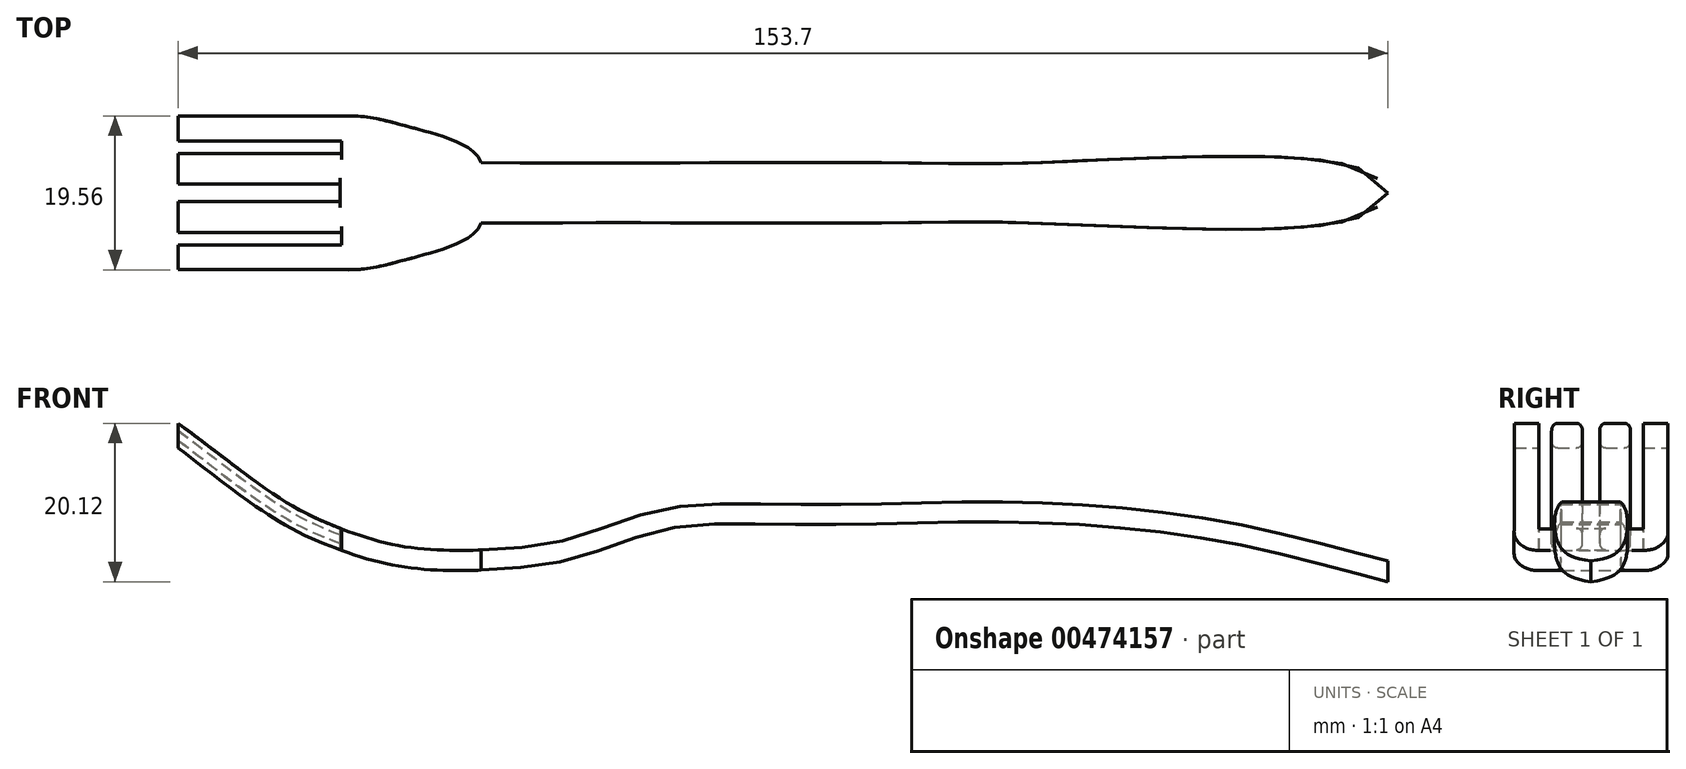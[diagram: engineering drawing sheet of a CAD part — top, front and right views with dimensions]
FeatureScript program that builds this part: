
annotation { "Feature Type Name" : "Feature", "Feature Type Description" : "" }
export const myFeature = defineFeature(function(context is Context, id is Id, definition is map)
    precondition{}
    {
        {
            var Q0;
            Q0=qCreatedBy(makeId("Front.planeOp"),FACE);
            var sketch = newSketch(context, id + "F0", { "sketchPlane" : qUnion([Q0])});
            skFitSpline(sketch, "E0", {"points": [v(0, 0) * mm, v(13.4, -9.82) * mm, v(20.96, -13.5) * mm, v(29.2, -15.74) * mm, v(40.7, -16) * mm, v(50.45, -14.5) * mm, v(61.2, -11) * mm, v(74.18, -10.24) * mm, v(88.18, -10.24) * mm, v(102.92, -10) * mm, v(119.66, -10.74) * mm, v(135.13, -12.92) * mm, v(150.68, -16.71) * mm, v(165.1, -21.65) * mm], "startDerivative": vector(162.7, -119.67) * mm, "endDerivative": vector(107.58, -72.4) * mm});
            skFitSpline(sketch, "E1.0", {"points": [v(-1.5, -2.05) * mm, v(0.16, -3.27) * mm, v(3.55, -5.87) * mm, v(7.68, -9) * mm, v(10.41, -10.92) * mm, v(11.92, -11.9) * mm, v(13.4, -12.8) * mm, v(15.14, -13.76) * mm, v(17.14, -14.7) * mm, v(18.76, -15.37) * mm, v(20.04, -15.86) * mm, v(21.35, -16.34) * mm, v(23.05, -16.93) * mm, v(25.24, -17.56) * mm, v(27.19, -18) * mm, v(28.84, -18.26) * mm, v(30.54, -18.48) * mm, v(32.71, -18.64) * mm, v(35.37, -18.7) * mm, v(38, -18.67) * mm, v(40.14, -18.57) * mm, v(41.79, -18.47) * mm, v(43.41, -18.35) * mm, v(45.41, -18.14) * mm, v(47.8, -17.76) * mm, v(49.59, -17.37) * mm, v(50.79, -17.04) * mm, v(51.6, -16.8) * mm, v(52.99, -16.36) * mm, v(54.93, -15.65) * mm, v(56.85, -14.94) * mm, v(58.36, -14.42) * mm, v(59.5, -14.06) * mm, v(60.63, -13.73) * mm, v(61.75, -13.46) * mm, v(62.89, -13.25) * mm, v(64.46, -13.02) * mm, v(66.5, -12.84) * mm, v(69.04, -12.75) * mm, v(71.24, -12.75) * mm, v(73.04, -12.77) * mm, v(74.85, -12.8) * mm, v(77.14, -12.82) * mm, v(79.89, -12.83) * mm, v(82.65, -12.84) * mm, v(85.41, -12.82) * mm, v(88.19, -12.79) * mm, v(90.96, -12.73) * mm, v(93.74, -12.66) * mm, v(96.53, -12.6) * mm, v(99.34, -12.55) * mm, v(102.19, -12.53) * mm, v(105.1, -12.55) * mm, v(109.03, -12.63) * mm, v(114.02, -12.85) * mm, v(119.97, -13.29) * mm, v(124.76, -13.8) * mm, v(128.5, -14.33) * mm, v(131.29, -14.78) * mm, v(134.03, -15.28) * mm, v(136.75, -15.85) * mm, v(139.48, -16.47) * mm, v(142.24, -17.15) * mm, v(145.06, -17.87) * mm, v(147.5, -18.5) * mm, v(149.5, -19.03) * mm, v(151.55, -19.56) * mm, v(154.13, -20.24) * mm, v(157.13, -21.08) * mm, v(159.87, -21.96) * mm, v(162.17, -22.87) * mm, v(163.28, -23.48) * mm, v(163.68, -23.75) * mm]});
            skLineSegment(sketch, "E2", {"start": v(-1.5, -2.05) * mm, "end": v(0, 0) * mm});
            skLineSegment(sketch, "E3", {"start": v(163.68, -23.75) * mm, "end": v(165.1, -21.65) * mm});
            skSolve(sketch);
        }
        {
            var Q0;
            Q0 = qSketchRegion(id + "F0", true);
            extrude(context, id + "F1", {"entities" : qUnion([Q0]), "depth" : 25.4 * mm});
        }
        {
            var Q0;
            Q0=qCreatedBy(makeId("Top.planeOp"),FACE);
            var sketch = newSketch(context, id + "F2", { "sketchPlane" : qUnion([Q0])});
            skPoint(sketch, "E4.0", {"position": v(0, -12.7) * mm});
            skLineSegment(sketch, "E5", {"start": v(0, -12.7) * mm, "end": v(165.1, -12.7) * mm});
            skPoint(sketch, "E6.0", {"position": v(165.1, -12.7) * mm});
            skLineSegment(sketch, "E7", {"start": v(20.57, -12.7) * mm, "end": v(20.57, -13.8) * mm});
            skLineSegment(sketch, "E8", {"start": v(20.57, -13.8) * mm, "end": v(0, -13.8) * mm});
            skLineSegment(sketch, "E9", {"start": v(0, -13.8) * mm, "end": v(0, -17.71) * mm});
            skLineSegment(sketch, "E10", {"start": v(0, -17.71) * mm, "end": v(20.73, -17.71) * mm});
            skLineSegment(sketch, "E11", {"start": v(20.73, -17.71) * mm, "end": v(20.73, -19.3) * mm});
            skLineSegment(sketch, "E12", {"start": v(20.73, -19.3) * mm, "end": v(0, -19.3) * mm});
            skLineSegment(sketch, "E13", {"start": v(0, -19.3) * mm, "end": v(0, -22.44) * mm});
            skLineSegment(sketch, "E14", {"start": v(0, -22.44) * mm, "end": v(20.73, -22.44) * mm});
            skFitSpline(sketch, "E15", {"points": [v(38.45, -16.52) * mm, v(67.46, -16.52) * mm, v(91.11, -16.52) * mm, v(108.25, -16.52) * mm, v(147.28, -16.52) * mm, v(153.7, -12.7) * mm, v(154.2, -6.84) * mm], "startDerivative": vector(190.89, 0.22) * mm, "endDerivative": vector(-3.36, 70.5) * mm});
            skFitSpline(sketch, "E16.MirrorCS", {"points": [v(38.45, -8.88) * mm, v(67.46, -8.88) * mm, v(91.11, -8.88) * mm, v(108.25, -8.88) * mm, v(147.28, -8.88) * mm, v(153.7, -12.7) * mm, v(154.2, -18.56) * mm], "startDerivative": vector(190.89, -0.22) * mm, "endDerivative": vector(-3.36, -70.5) * mm});
            skLineSegment(sketch, "E17.MirrorCS", {"start": v(0, -6.1) * mm, "end": v(0, -2.96) * mm});
            skLineSegment(sketch, "E18.MirrorCS", {"start": v(0, -11.6) * mm, "end": v(0, -7.69) * mm});
            skLineSegment(sketch, "E19.MirrorCS", {"start": v(20.73, -7.69) * mm, "end": v(20.73, -6.1) * mm});
            skLineSegment(sketch, "E20.MirrorCS", {"start": v(20.57, -12.7) * mm, "end": v(20.57, -11.6) * mm});
            skLineSegment(sketch, "E21.MirrorCS", {"start": v(20.57, -11.6) * mm, "end": v(0, -11.6) * mm});
            skLineSegment(sketch, "E22.MirrorCS", {"start": v(0, -7.69) * mm, "end": v(20.73, -7.69) * mm});
            skLineSegment(sketch, "E23.MirrorCS", {"start": v(0, -2.96) * mm, "end": v(20.73, -2.96) * mm});
            skLineSegment(sketch, "E24.MirrorCS", {"start": v(20.73, -6.1) * mm, "end": v(0, -6.1) * mm});
            skLineSegment(sketch, "E25", {"start": v(-14.1, 17.07) * mm, "end": v(-14.1, -45.05) * mm});
            skLineSegment(sketch, "E26", {"start": v(-14.1, -45.05) * mm, "end": v(184.94, -45.05) * mm});
            skLineSegment(sketch, "E27", {"start": v(184.94, -45.05) * mm, "end": v(184.94, 20.3) * mm});
            skLineSegment(sketch, "E28", {"start": v(184.94, 20.3) * mm, "end": v(-14.1, 17.07) * mm});
            skFitSpline(sketch, "E29", {"points": [v(20.73, -22.44) * mm, v(29.3, -21.1) * mm, v(38.45, -16.52) * mm], "startDerivative": vector(18.66, -1.22) * mm, "endDerivative": vector(3.59, 13.59) * mm});
            skFitSpline(sketch, "E30.MirrorCS", {"points": [v(20.73, -2.96) * mm, v(29.3, -4.3) * mm, v(38.45, -8.88) * mm], "startDerivative": vector(18.66, 1.22) * mm, "endDerivative": vector(3.59, -13.59) * mm});
            skSolve(sketch);
        }
        {
            var Q0;
            Q0=makeQuery(id+"F2.imprint","IMPRINT",FACE,{"disambiguationData":[TD([[makeQuery(id+"F2.imprint","IMPRINT",EDGE,{"derivedFrom":sQuery(id+"F2.wireOp",EDGE,"E7")}),-1.0]])]});
            extrude(context, id + "F3", {"entities" : qUnion([Q0]), "operationType" : NewBodyOperationType.REMOVE, "oppositeDirection" : true, "depth" : 25.9 * mm});
        }
        {
            var Q0;
            Q0=makeQuery(id+"F3.boolean.opBoolean","INTERSECT",EDGE,{"derivedFrom":[makeQuery(id+"F1.opExtrude","SWEPT_FACE",FACE,{"disambiguationData":[OSD([sQuery(id+"F0.wireOp",EDGE,"E0")])]}),makeQuery(id+"F3.opExtrude","SWEPT_FACE",FACE,{"disambiguationData":[OSD([sQuery(id+"F2.wireOp",EDGE,"E10")])]})]});
            var Q1;
            Q1=makeQuery(id+"F3.boolean.opBoolean","INTERSECT",EDGE,{"derivedFrom":[makeQuery(id+"F1.opExtrude","SWEPT_FACE",FACE,{"disambiguationData":[OSD([sQuery(id+"F0.wireOp",EDGE,"E0")])]}),makeQuery(id+"F3.opExtrude","SWEPT_FACE",FACE,{"disambiguationData":[OSD([sQuery(id+"F2.wireOp",EDGE,"E8")])]})]});
            var Q2;
            Q2=makeQuery(id+"F3.boolean.opBoolean","INTERSECT",EDGE,{"derivedFrom":[makeQuery(id+"F1.opExtrude","SWEPT_FACE",FACE,{"disambiguationData":[OSD([sQuery(id+"F0.wireOp",EDGE,"E1.0")])]}),makeQuery(id+"F3.opExtrude","SWEPT_FACE",FACE,{"disambiguationData":[OSD([sQuery(id+"F2.wireOp",EDGE,"E8")])]})]});
            var Q3;
            Q3=makeQuery(id+"F3.boolean.opBoolean","INTERSECT",EDGE,{"derivedFrom":[makeQuery(id+"F1.opExtrude","SWEPT_FACE",FACE,{"disambiguationData":[OSD([sQuery(id+"F0.wireOp",EDGE,"E1.0")])]}),makeQuery(id+"F3.opExtrude","SWEPT_FACE",FACE,{"disambiguationData":[OSD([sQuery(id+"F2.wireOp",EDGE,"E21.MirrorCS")])]})]});
            var Q4;
            Q4=makeQuery(id+"F3.boolean.opBoolean","INTERSECT",EDGE,{"derivedFrom":[makeQuery(id+"F1.opExtrude","SWEPT_FACE",FACE,{"disambiguationData":[OSD([sQuery(id+"F0.wireOp",EDGE,"E1.0")])]}),makeQuery(id+"F3.opExtrude","SWEPT_FACE",FACE,{"disambiguationData":[OSD([sQuery(id+"F2.wireOp",EDGE,"E10")])]})]});
            var Q5;
            Q5=makeQuery(id+"F3.boolean.opBoolean","INTERSECT",EDGE,{"derivedFrom":[makeQuery(id+"F1.opExtrude","SWEPT_FACE",FACE,{"disambiguationData":[OSD([sQuery(id+"F0.wireOp",EDGE,"E1.0")])]}),makeQuery(id+"F3.opExtrude","SWEPT_FACE",FACE,{"disambiguationData":[OSD([sQuery(id+"F2.wireOp",EDGE,"E22.MirrorCS")])]})]});
            var Q6;
            Q6=makeQuery(id+"F3.boolean.opBoolean","INTERSECT",EDGE,{"derivedFrom":[makeQuery(id+"F1.opExtrude","SWEPT_FACE",FACE,{"disambiguationData":[OSD([sQuery(id+"F0.wireOp",EDGE,"E0")])]}),makeQuery(id+"F3.opExtrude","SWEPT_FACE",FACE,{"disambiguationData":[OSD([sQuery(id+"F2.wireOp",EDGE,"E21.MirrorCS")])]})]});
            var Q7;
            Q7=makeQuery(id+"F3.boolean.opBoolean","INTERSECT",EDGE,{"derivedFrom":[makeQuery(id+"F1.opExtrude","SWEPT_FACE",FACE,{"disambiguationData":[OSD([sQuery(id+"F0.wireOp",EDGE,"E0")])]}),makeQuery(id+"F3.opExtrude","SWEPT_FACE",FACE,{"disambiguationData":[OSD([sQuery(id+"F2.wireOp",EDGE,"E22.MirrorCS")])]})]});
            fillet(context, id + "F4", {"entities" : qUnion([Q0, Q1, Q2, Q3, Q4, Q5, Q6, Q7]), "radius" : 0.76 * mm, "tangentPropagation" : true, "allowEdgeOverflow" : false});
        }
    });
